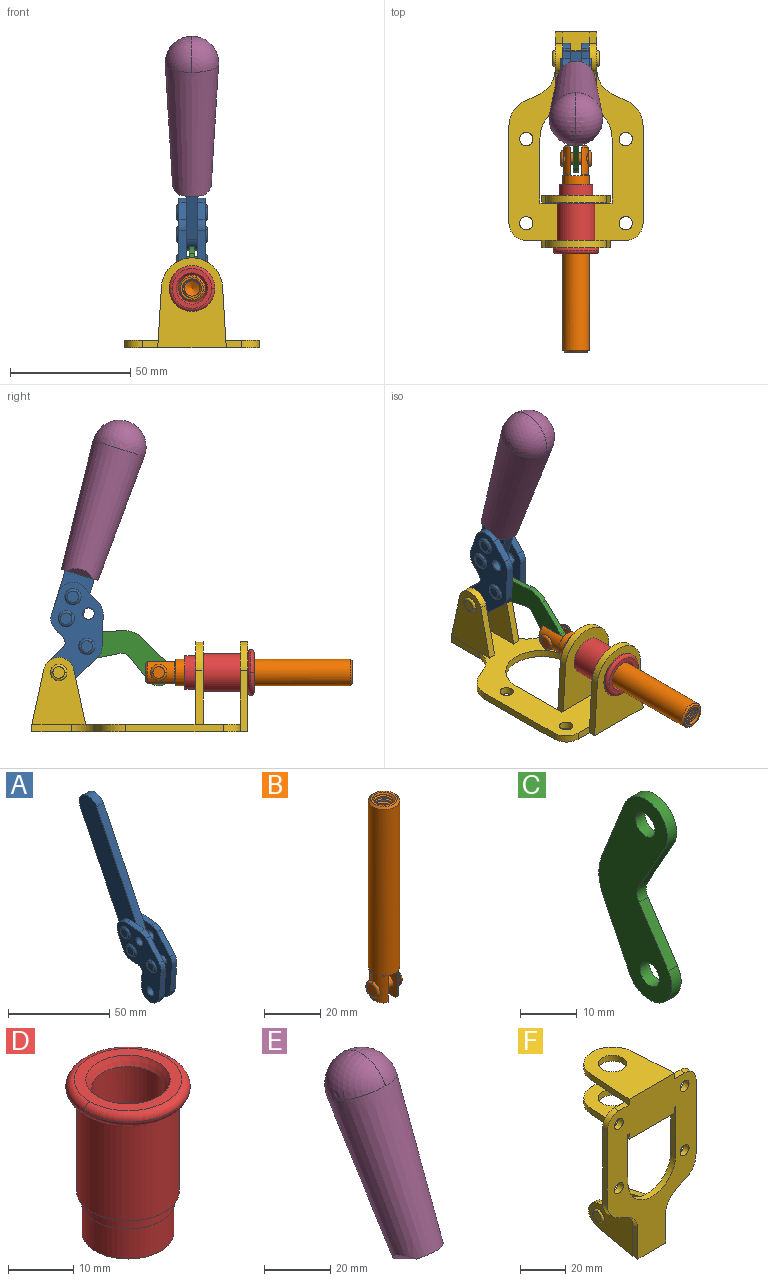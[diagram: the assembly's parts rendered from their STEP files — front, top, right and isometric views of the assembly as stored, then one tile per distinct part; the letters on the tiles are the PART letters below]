
ASSEMBLY  parts=6 mates=6
PART A: 59 faces, bbox 12.9x60.2x99.6 mm
  f0: torus R=2.39mm, axis (-1,0,0), area 14.9mm2, adj f20,f43,f51
  f1: torus R=2.39mm, axis (-1,0,0), area 14.9mm2, adj f19,f42,f51
  f2: torus R=2.39mm, axis (-1,0,0), area 14.9mm2, adj f18,f35,f51
  f3: torus R=2.39mm, axis (-1,0,0), area 14.9mm2, adj f14,f17,f23
  f4: torus R=2.39mm, axis (-1,0,0), area 14.9mm2, adj f13,f16,f23
  f5: torus R=2.39mm, axis (-1,0,0), area 14.9mm2, adj f12,f15,f23
  f6: cylinder r=2.39mm len=4.78mm, axis (1,0,0), area 46.5mm2, adj f48,f50,f51
  f7: cylinder r=2.39mm len=4.78mm, axis (1,0,0), area 46.5mm2, adj f50,f51
  f8: cylinder r=6.35mm len=12.68mm, axis (1,0,0), area 61.8mm2, adj f38,f39,f50,f51
  f9: cylinder r=2.39mm len=4.78mm, axis (-1,0,0), area 70.5mm2, adj f46,f50
  f10: cylinder r=2.39mm len=4.78mm, axis (-1,0,0), area 46.5mm2, adj f23,f45,f46
  f11: cylinder r=2.39mm len=4.78mm, axis (-1,0,0), area 46.5mm2, adj f23,f46
  f12: plane 4.78x4.78mm, normal (1,0,0), area 17.9mm2, adj f5,f15
  f13: plane 4.78x4.78mm, normal (1,0,0), area 17.9mm2, adj f4,f16
  f14: plane 4.78x4.78mm, normal (1,0,0), area 17.9mm2, adj f3,f17
  f15: torus R=2.39mm, axis (-1,0,0), area 14.9mm2, adj f5,f12,f23
  f16: torus R=2.39mm, axis (-1,0,0), area 14.9mm2, adj f4,f13,f23
  f17: torus R=2.39mm, axis (-1,0,0), area 14.9mm2, adj f3,f14,f23
  f18: plane 4.78x4.78mm, normal (-1,0,0), area 17.9mm2, adj f2,f35
  f19: plane 4.78x4.78mm, normal (-1,0,0), area 17.9mm2, adj f1,f42
  f20: plane 4.78x4.78mm, normal (-1,0,0), area 17.9mm2, adj f0,f43
  f21: plane 2.26x0.2mm, normal (1,0,0), area 0.2mm2, adj f31,f44
  f22: plane 2.26x0.2mm, normal (-1,0,0), area 0.2mm2, adj f41,f44
  f23: plane 39.37x30.77mm, normal (1,0,0), area 565.5mm2, adj f3,f4,f5,f10,f11,f15,f16,f17
  f24: cylinder r=6.1mm len=4.15mm, axis (-1,0,0), area 14.7mm2, adj f23,f25,f32,f46
  f25: plane 10.25x9.01mm, normal (0,-0.75,0.66), area 42.3mm2, adj f23,f24,f26,f46
  f26: cylinder r=6.35mm len=4.64mm, axis (-1,0,0), area 15.6mm2, adj f23,f25,f27,f46
  f27: plane 15.84x3.1mm, normal (0,-1,-0.07), area 49.2mm2, adj f23,f26,f28,f46
  f28: cylinder r=6.35mm len=12.68mm, axis (-1,0,0), area 61.8mm2, adj f23,f27,f29,f46
  f29: plane 8.11x3.1mm, normal (0,1,0.07), area 25.2mm2, adj f23,f28,f30,f46
  f30: cylinder r=3.05mm len=3.25mm, axis (-1,0,0), area 14.8mm2, adj f23,f29,f31,f46
  f31: plane 5.99x3.1mm, normal (0,0.07,-1), area 18.6mm2, adj f21,f23,f30,f44,f46
  f32: plane 9.5x3.1mm, normal (0,-0.07,1), area 29.5mm2, adj f23,f24,f33,f46,f47
  f33: cylinder r=6.1mm len=8.63mm, axis (-1,0,0), area 39.1mm2, adj f23,f32,f34,f47
  f34: plane 8.65x3.96mm, normal (0,0.91,-0.42), area 29.5mm2, adj f23,f33,f44,f47
  f35: torus R=2.39mm, axis (-1,0,0), area 14.9mm2, adj f2,f18,f51
  f36: plane 10.25x9.01mm, normal (0,-0.75,0.66), area 42.3mm2, adj f37,f49,f50,f51
  f37: cylinder r=6.35mm len=4.64mm, axis (1,0,0), area 15.6mm2, adj f36,f38,f50,f51
  f38: plane 15.84x3.1mm, normal (0,-1,-0.07), area 49.2mm2, adj f8,f37,f50,f51
  f39: plane 8.11x3.1mm, normal (0,1,0.07), area 25.2mm2, adj f8,f40,f50,f51
  f40: cylinder r=3.05mm len=3.25mm, axis (1,0,0), area 14.8mm2, adj f39,f41,f50,f51
  f41: plane 5.99x3.1mm, normal (0,0.07,-1), area 18.6mm2, adj f22,f40,f44,f50,f51
  f42: torus R=2.39mm, axis (-1,0,0), area 14.9mm2, adj f1,f19,f51
  f43: torus R=2.39mm, axis (-1,0,0), area 14.9mm2, adj f0,f20,f51
  f44: cylinder r=6.35mm len=12.12mm, axis (-1,0,0), area 128.9mm2, adj f21,f22,f23,f31,f34,f41,f46,f47
  f45: plane 2.65x1.35mm, normal (1,0,0), area 1mm2, adj f10,f55
  f46: plane 39.08x20.42mm, normal (-1,0,0), area 412.5mm2, adj f9,f10,f11,f24,f25,f26,f27,f28
  f47: plane 77.62x39.82mm, normal (1,0,0), area 850mm2, adj f32,f33,f34,f44,f53,f54,f55
  f48: plane 2.65x1.35mm, normal (-1,0,0), area 1mm2, adj f6,f55
  f49: cylinder r=6.1mm len=4.15mm, axis (1,0,0), area 14.7mm2, adj f36,f50,f51,f56
  f50: plane 39.08x20.42mm, normal (1,0,0), area 412.5mm2, adj f6,f7,f8,f9,f36,f37,f38,f39
  f51: plane 39.37x30.77mm, normal (-1,0,0), area 565.5mm2, adj f0,f1,f2,f6,f7,f8,f35,f36
  f52: plane 8.65x3.96mm, normal (0,0.91,-0.42), area 29.5mm2, adj f44,f51,f57,f58
  f53: plane 68.49x33.4mm, normal (0,0.9,-0.44), area 358.1mm2, adj f44,f47,f54,f58
  f54: cylinder r=6.35mm len=12.06mm, axis (1,0,0), area 93.7mm2, adj f47,f53,f55,f58
  f55: plane 68.49x33.4mm, normal (0,-0.9,0.44), area 358.1mm2, adj f44,f45,f46,f47,f48,f50,f54,f58
  f56: plane 9.5x3.1mm, normal (0,-0.07,1), area 29.5mm2, adj f49,f50,f51,f57,f58
  f57: cylinder r=6.1mm len=8.63mm, axis (1,0,0), area 39.1mm2, adj f51,f52,f56,f58
  f58: plane 77.62x39.82mm, normal (-1,0,0), area 850mm2, adj f44,f52,f53,f54,f55,f56,f57
PART B: 48 faces, bbox 12.6x11.1x86.1 mm
  f0: torus R=2.41mm, axis (-1,0,0), area 15mm2, adj f30,f32,f34
  f1: torus R=2.41mm, axis (-1,0,0), area 15mm2, adj f29,f31,f33
  f2: cylinder r=5.54mm len=72.39mm, axis (0,0,1), area 2518.5mm2, adj f3,f4,f42,f43
  f3: cone r=5.54mm half-angle=45deg, axis (0,0,1), area 7.6mm2, adj f2,f5,f41
  f4: cone r=5.54mm half-angle=45deg, axis (0,0,-1), area 34.9mm2, adj f2,f39
  f5: cylinder r=5.08mm len=11.48mm, axis (0,0,1), area 108.3mm2, adj f3,f7,f8,f41
  f6: cylinder r=2.41mm len=4.83mm, axis (-1,0,0), area 71.2mm2, adj f40,f41
  f7: cylinder r=2.41mm len=4.83mm, axis (-1,0,0), area 7.6mm2, adj f5,f34
  f8: cone r=5.08mm half-angle=45deg, axis (0,0,1), area 10.6mm2, adj f5,f37,f41
  f9: cone r=3.98mm half-angle=45deg, axis (0,0,1), area 17.6mm2, adj f27,f39,f45,f46,f47
  f10: cylinder r=2.41mm len=4.83mm, axis (-1,0,0), area 7.6mm2, adj f33,f38
  f11: cylinder r=3.2mm len=6.4mm, axis (0,0,1), area 78.4mm2, adj f12,f28,f44,f45,f47
  f12: cylinder r=3.2mm len=6.4mm, axis (0,0,1), area 10.5mm2, adj f11,f13,f45,f47
  f13: cylinder r=3.2mm len=6.4mm, axis (0,0,1), area 10.5mm2, adj f12,f14,f45,f47
  f14: cylinder r=3.2mm len=6.4mm, axis (0,0,1), area 10.5mm2, adj f13,f15,f45,f47
  f15: cylinder r=3.2mm len=6.4mm, axis (0,0,1), area 10.5mm2, adj f14,f16,f45,f47
  f16: cylinder r=3.2mm len=6.4mm, axis (0,0,1), area 10.5mm2, adj f15,f17,f45,f47
  f17: cylinder r=3.2mm len=6.4mm, axis (0,0,1), area 10.5mm2, adj f16,f18,f45,f47
  f18: cylinder r=3.2mm len=6.4mm, axis (0,0,1), area 10.5mm2, adj f17,f19,f45,f47
  f19: cylinder r=3.2mm len=6.4mm, axis (0,0,1), area 10.5mm2, adj f18,f20,f45,f47
  f20: cylinder r=3.2mm len=6.4mm, axis (0,0,1), area 10.5mm2, adj f19,f21,f45,f47
  f21: cylinder r=3.2mm len=6.4mm, axis (0,0,1), area 10.5mm2, adj f20,f22,f45,f47
  f22: cylinder r=3.2mm len=6.4mm, axis (0,0,1), area 10.5mm2, adj f21,f23,f45,f47
  f23: cylinder r=3.2mm len=6.4mm, axis (0,0,1), area 10.5mm2, adj f22,f24,f45,f47
  f24: cylinder r=3.2mm len=6.4mm, axis (0,0,1), area 10.5mm2, adj f23,f25,f45,f47
  f25: cylinder r=3.2mm len=6.4mm, axis (0,0,1), area 10.5mm2, adj f24,f26,f45,f47
  f26: cylinder r=3.2mm len=6.4mm, axis (0,0,1), area 10.5mm2, adj f25,f27,f45,f47
  f27: cylinder r=3.2mm len=6.4mm, axis (0,0,1), area 7.4mm2, adj f9,f26,f45,f47
  f28: cone r=3.2mm half-angle=60deg, axis (0,0,1), area 37.2mm2, adj f11
  f29: plane 4.83x4.83mm, normal (-1,0,0), area 18.3mm2, adj f1,f31
  f30: plane 4.83x4.83mm, normal (1,0,0), area 18.3mm2, adj f0,f32
  f31: torus R=2.41mm, axis (-1,0,0), area 15mm2, adj f1,f29,f33
  f32: torus R=2.41mm, axis (-1,0,0), area 15mm2, adj f0,f30,f34
  f33: plane 6.83x6.83mm, normal (1,0,0), area 18.3mm2, adj f1,f10,f31
  f34: plane 6.83x6.83mm, normal (-1,0,0), area 18.3mm2, adj f0,f7,f32
  f35: cone r=5.08mm half-angle=45deg, axis (0,0,1), area 10.6mm2, adj f36,f38,f40
  f36: plane 7.25x1.97mm, normal (0,0,-1), area 10mm2, adj f35,f40
  f37: plane 7.25x1.97mm, normal (0,0,-1), area 10mm2, adj f8,f41
  f38: cylinder r=5.08mm len=11.48mm, axis (0,0,1), area 108.3mm2, adj f10,f35,f40,f42
  f39: plane 9.55x9.55mm, normal (0,0,1), area 22mm2, adj f4,f9
  f40: plane 12.76x10.09mm, normal (1,0,0), area 95.7mm2, adj f6,f35,f36,f38,f42,f43
  f41: plane 12.76x10.09mm, normal (-1,0,0), area 95.7mm2, adj f3,f5,f6,f8,f37,f43
  f42: cone r=5.54mm half-angle=45deg, axis (0,0,1), area 7.6mm2, adj f2,f38,f40
  f43: plane 11.07x4.7mm, normal (0,0,-1), area 50.4mm2, adj f2,f40,f41
  f44: plane 0.89x0.62mm, normal (-1,0,0), area 0.3mm2, adj f11,f45,f46,f47
  f45: bspline ~24.8x7.63mm, area 266.6mm2, adj f9,f11,f12,f13,f14,f15,f16,f17
  f46: bspline ~24.87x7.63mm, area 73.6mm2, adj f9,f44,f45,f47
  f47: bspline ~24.98x7.63mm, area 272.5mm2, adj f9,f11,f12,f13,f14,f15,f16,f17
PART C: 12 faces, bbox 2.3x18.2x42.8 mm
  f0: cylinder r=2.4mm len=4.8mm, axis (1,0,0), area 34.9mm2, adj f4,f11
  f1: cylinder r=10.41mm len=8.47mm, axis (1,0,0), area 20.2mm2, adj f4,f9,f10,f11
  f2: cylinder r=3.05mm len=3.16mm, axis (1,0,0), area 7.7mm2, adj f4,f6,f7,f11
  f3: cylinder r=2.4mm len=4.8mm, axis (1,0,0), area 34.9mm2, adj f4,f11
  f4: plane 42.81x18.23mm, normal (-1,0,0), area 414.1mm2, adj f0,f1,f2,f3,f5,f6,f7,f8
  f5: cylinder r=5.54mm len=10.67mm, axis (1,0,0), area 41.8mm2, adj f4,f6,f10,f11
  f6: plane 11.66x6.53mm, normal (0,-0.87,-0.49), area 30.9mm2, adj f2,f4,f5,f11
  f7: plane 11.17x7.33mm, normal (0,-0.84,0.55), area 30.9mm2, adj f2,f4,f8,f11
  f8: cylinder r=5.54mm len=10.51mm, axis (1,0,0), area 41.8mm2, adj f4,f7,f9,f11
  f9: plane 13.67x6.67mm, normal (0,0.9,-0.44), area 35.1mm2, adj f1,f4,f8,f11
  f10: plane 14.1x5.7mm, normal (0,0.93,0.37), area 35.1mm2, adj f1,f4,f5,f11
  f11: plane 42.81x18.23mm, normal (1,0,0), area 414.1mm2, adj f0,f1,f2,f3,f5,f6,f7,f8
PART D: 15 faces, bbox 20.6x20.6x28.7 mm
  f0: torus R=8.26mm, axis (0,0,1), area 56.8mm2, adj f1,f10,f12
  f1: torus R=8.26mm, axis (0,0,1), area 56.8mm2, adj f0,f6,f13
  f2: cylinder r=5.59mm len=25.91mm, axis (0,0,1), area 909.6mm2, adj f3,f4
  f3: cone r=6.86mm half-angle=45deg, axis (0,0,-1), area 70.2mm2, adj f2,f14
  f4: cone r=6.47mm half-angle=30deg, axis (0,0,1), area 66.7mm2, adj f2,f13
  f5: cylinder r=7.04mm len=14.07mm, axis (0,0,1), area 252.6mm2, adj f11,f14
  f6: torus R=8.26mm, axis (0,0,1), area 56.8mm2, adj f1,f12,f13
  f7: cylinder r=7.16mm len=14.33mm, axis (0,0,1), area 91.5mm2, adj f9,f11
  f8: cylinder r=7.86mm len=18.42mm, axis (0,0,1), area 909.6mm2, adj f9,f10
  f9: plane 15.72x15.72mm, normal (0,0,-1), area 33mm2, adj f7,f8
  f10: plane 16.51x16.51mm, normal (0,0,-1), area 19.9mm2, adj f0,f8,f12
  f11: plane 14.33x14.33mm, normal (0,0,-1), area 5.7mm2, adj f5,f7
  f12: torus R=8.26mm, axis (0,0,1), area 56.8mm2, adj f0,f6,f10
  f13: plane 16.51x16.51mm, normal (0,0,1), area 82.7mm2, adj f1,f4,f6
  f14: plane 14.07x14.07mm, normal (0,0,-1), area 7.8mm2, adj f3,f5
PART E: 11 faces, bbox 22.3x42.6x64.5 mm
  f0: sphere r=11.13mm, area 411.4mm2, adj f1,f8
  f1: cone r=11.11mm half-angle=3.3deg, axis (0,0.44,0.9), area 3251.8mm2, adj f0,f7,f8,f9,f10
  f2: cylinder r=6.16mm len=11.7mm, axis (1,0,0), area 89.5mm2, adj f3,f4,f5,f6
  f3: plane 60.23x36.75mm, normal (-1,0,0), area 763.6mm2, adj f2,f4,f6,f10
  f4: plane 51.37x25.05mm, normal (0,0.9,-0.44), area 264.2mm2, adj f2,f3,f5,f10
  f5: plane 60.23x36.75mm, normal (1,0,0), area 763.6mm2, adj f2,f4,f6,f10
  f6: plane 51.37x25.05mm, normal (0,-0.9,0.44), area 264.2mm2, adj f2,f3,f5,f10
  f7: plane 9.95x5.95mm, normal (0.71,-0.31,-0.64), area 25.8mm2, adj f1,f10
  f8: sphere r=11.13mm, area 411.4mm2, adj f0,f1
  f9: plane 9.95x5.95mm, normal (-0.71,-0.31,-0.64), area 25.8mm2, adj f1,f10
  f10: plane 14.27x11.38mm, normal (0,-0.44,-0.9), area 106.7mm2, adj f1,f3,f4,f5,f6,f7,f9
PART F: 55 faces, bbox 55.7x37.4x89.8 mm
  f0: torus R=2.41mm, axis (-1,0,0), area 15mm2, adj f11,f15,f25
  f1: torus R=2.41mm, axis (-1,0,0), area 15mm2, adj f10,f12,f22
  f2: cylinder r=2.78mm len=5.56mm, axis (0,-1,0), area 54.2mm2, adj f30,f54
  f3: cylinder r=14.99mm len=29.97mm, axis (0,-1,0), area 145.9mm2, adj f30,f49,f53,f54
  f4: cylinder r=2.78mm len=5.56mm, axis (0,-1,0), area 54.2mm2, adj f30,f54
  f5: cylinder r=2.78mm len=5.56mm, axis (0,-1,0), area 54.2mm2, adj f30,f54
  f6: cylinder r=2.78mm len=5.56mm, axis (0,-1,0), area 54.2mm2, adj f30,f54
  f7: cylinder r=6.35mm len=12.7mm, axis (0,0,1), area 123.6mm2, adj f27,f51
  f8: cylinder r=6.35mm len=12.7mm, axis (0,0,-1), area 124.7mm2, adj f21,f35
  f9: cylinder r=2.41mm len=11.18mm, axis (-1,0,0), area 169.4mm2, adj f16,f19
  f10: plane 4.83x4.83mm, normal (1,0,0), area 18.3mm2, adj f1,f12
  f11: plane 4.83x4.83mm, normal (-1,0,0), area 18.3mm2, adj f0,f15
  f12: torus R=2.41mm, axis (-1,0,0), area 15mm2, adj f1,f10,f22
  f13: cylinder r=6.35mm len=12.41mm, axis (1,0,0), area 53.4mm2, adj f18,f19,f22,f23
  f14: cylinder r=6.35mm len=12.41mm, axis (-1,0,0), area 53.4mm2, adj f16,f17,f24,f25
  f15: torus R=2.41mm, axis (-1,0,0), area 15mm2, adj f0,f11,f25
  f16: plane 27.86x22.35mm, normal (1,0,0), area 425.4mm2, adj f9,f14,f17,f24,f30
  f17: plane 22.86x4.97mm, normal (0,0.21,0.98), area 72.5mm2, adj f14,f16,f25,f30
  f18: plane 22.86x4.97mm, normal (0,0.21,0.98), area 72.5mm2, adj f13,f19,f22,f30
  f19: plane 27.86x22.35mm, normal (-1,0,0), area 425.4mm2, adj f9,f13,f18,f23,f30
  f20: cylinder r=12.7mm len=25.35mm, axis (0,0,-1), area 119.8mm2, adj f21,f34,f35,f36
  f21: plane 34.21x28.07mm, normal (0,0,-1), area 702.4mm2, adj f8,f20,f30,f34,f36
  f22: plane 27.96x22.45mm, normal (1,0,0), area 407.2mm2, adj f1,f12,f13,f18,f23,f30,f42,f43
  f23: plane 22.86x4.97mm, normal (0,0.21,-0.98), area 72.5mm2, adj f13,f19,f22,f44
  f24: plane 22.86x4.97mm, normal (0,0.21,-0.98), area 72.5mm2, adj f14,f16,f25,f44
  f25: plane 27.86x22.35mm, normal (-1,0,0), area 407.1mm2, adj f0,f14,f15,f17,f24,f30,f45,f46
  f26: plane 3.1x0.95mm, normal (0,0,-1), area 2.7mm2, adj f30,f49,f50,f54
  f27: plane 34.21x28.07mm, normal (0,0,1), area 702.4mm2, adj f7,f28,f30,f50,f52
  f28: cylinder r=12.7mm len=25.35mm, axis (0,0,1), area 118.8mm2, adj f27,f50,f51,f52
  f29: plane 3.1x0.95mm, normal (0,0,-1), area 2.7mm2, adj f30,f52,f53,f54
  f30: plane 86.54x55.63mm, normal (0,1,0), area 2362.9mm2, adj f2,f3,f4,f5,f6,f16,f17,f18
  f31: plane 40.56x3.1mm, normal (-1,0,0), area 125.7mm2, adj f30,f32,f48,f54
  f32: cylinder r=7.11mm len=7.11mm, axis (0,-1,0), area 34.6mm2, adj f30,f31,f33,f54
  f33: plane 6.67x3.1mm, normal (0,0,1), area 20.4mm2, adj f30,f32,f34,f54
  f34: plane 25.39x3.13mm, normal (-1,0.06,0), area 79.5mm2, adj f20,f21,f33,f35,f54
  f35: plane 37.31x28.45mm, normal (0,0,1), area 789.9mm2, adj f8,f20,f34,f36,f54
  f36: plane 25.39x3.13mm, normal (1,0.06,0), area 79.5mm2, adj f20,f21,f35,f37,f54
  f37: plane 6.67x3.1mm, normal (0,0,1), area 20.4mm2, adj f30,f36,f38,f54
  f38: cylinder r=7.11mm len=7.11mm, axis (0,-1,0), area 34.6mm2, adj f30,f37,f39,f54
  f39: plane 40.56x3.1mm, normal (1,0,0), area 125.7mm2, adj f30,f38,f40,f54
  f40: cylinder r=11.18mm len=10.16mm, axis (0,-1,0), area 39.5mm2, adj f30,f39,f41,f54
  f41: plane 6.09x3.1mm, normal (0.42,0,-0.91), area 20.8mm2, adj f30,f40,f42,f54
  f42: cylinder r=11.18mm len=9.41mm, axis (0,-1,0), area 37.2mm2, adj f22,f30,f41,f43,f54
  f43: plane 16.5x3.1mm, normal (1,0,0), area 51.1mm2, adj f22,f42,f44,f54
  f44: plane 17.37x3.1mm, normal (0,0,-1), area 53.8mm2, adj f23,f24,f30,f43,f45,f54
  f45: plane 16.5x3.1mm, normal (-1,0,0), area 51.1mm2, adj f25,f44,f46,f54
  f46: cylinder r=11.18mm len=9.41mm, axis (0,-1,0), area 37.2mm2, adj f25,f30,f45,f47,f54
  f47: plane 6.09x3.1mm, normal (-0.42,0,-0.91), area 20.8mm2, adj f30,f46,f48,f54
  f48: cylinder r=11.18mm len=10.16mm, axis (0,-1,0), area 39.5mm2, adj f30,f31,f47,f54
  f49: plane 26.54x3.1mm, normal (-1,0,0), area 82.3mm2, adj f3,f26,f30,f54
  f50: plane 25.39x3.1mm, normal (1,0.06,0), area 78.8mm2, adj f26,f27,f28,f51,f54
  f51: plane 37.31x28.45mm, normal (0,0,-1), area 789.9mm2, adj f7,f28,f50,f52,f54
  f52: plane 25.39x3.1mm, normal (-1,0.06,0), area 78.8mm2, adj f27,f28,f29,f51,f54
  f53: plane 26.54x3.1mm, normal (1,0,0), area 82.3mm2, adj f3,f29,f30,f54
  f54: plane 89.66x55.63mm, normal (0,-1,0), area 2678.5mm2, adj f2,f3,f4,f5,f6,f26,f29,f31
PLACE A rot(axis=(1,0,0),43.2deg) t=(0,1.33,31.18)mm
PLACE B rot(axis=(1,0,0),90deg) t=(0,15.2,0)mm
PLACE C rot(axis=(1,0,0),111.9deg) t=(0,23.26,7.54)mm
PLACE D rot(axis=(1,0,0),90deg) t=(0,9.14,0)mm
PLACE E rot(axis=(1,0,0),43.2deg) t=(-0.04,1.33,31.18)mm
PLACE F rot(axis=(1,0,0),90deg) t=(0,9.14,0)mm fixed
MATE revolute C.f5 <-> B.f6  axis (1,0,0) through (0,-0.27,24.61)mm
MATE fastened E.f2 <-> A.f54  axis (1,0,0) through (-2.35,15.66,119.73)mm
MATE fastened D.f2 <-> F.f7  axis (0,1,0) through (0,-37.25,24.61)mm
MATE revolute F.f0 <-> A.f7  axis (-1,0,0) through (0,41.23,24.61)mm
MATE slider F.f7 <-> B.f2  axis (0,-1,0) through (0,-37.25,24.61)mm
MATE revolute C.f3 <-> A.f4  axis (1,0,0) through (0,29.59,35.4)mm
